# Revit family: Noon
name_source: partatom
category: Мебель
revit_build: Autodesk Revit 2017 (Build: 20160225_1515(x64)
units: mm (PartAtom-declared; Revit-internal decimal feet)

## family parameters
Всегда вертикально = Да
Заголовок OmniClass = General Furniture and Specialties
На основе рабочей плоскости = Нет
Номер OmniClass = 23.40.20.00
Общий = Нет
При загрузке вырезать с полостями = Нет
Точка расчета площади = Нет

## types (4) — shared parameters
Fabric = Skandiform Fabric
Leg = Skandiform Chrome
Изготовитель = Skandiform AB
Ключевая пометка = XBF.4
Комментарии к типоразмеру = Created by Astacus AB
Описание = Silver lacquered chassis.

## per-type parameters (varying)
| type | URL |
| SA-302 | http://www.biminfo.se |
| SA-303 | http://www.biminfo.se |
| SA-304 | http://www.biminfo.se |
| SA-305 | http://file-system.ru |

note: column(s) folded — value = type name in every type: Type, Группа модели

## geometry (parser evidence)
native form markers: Blend x2, Sweep x15
no freeform markers — native parametric forms only
